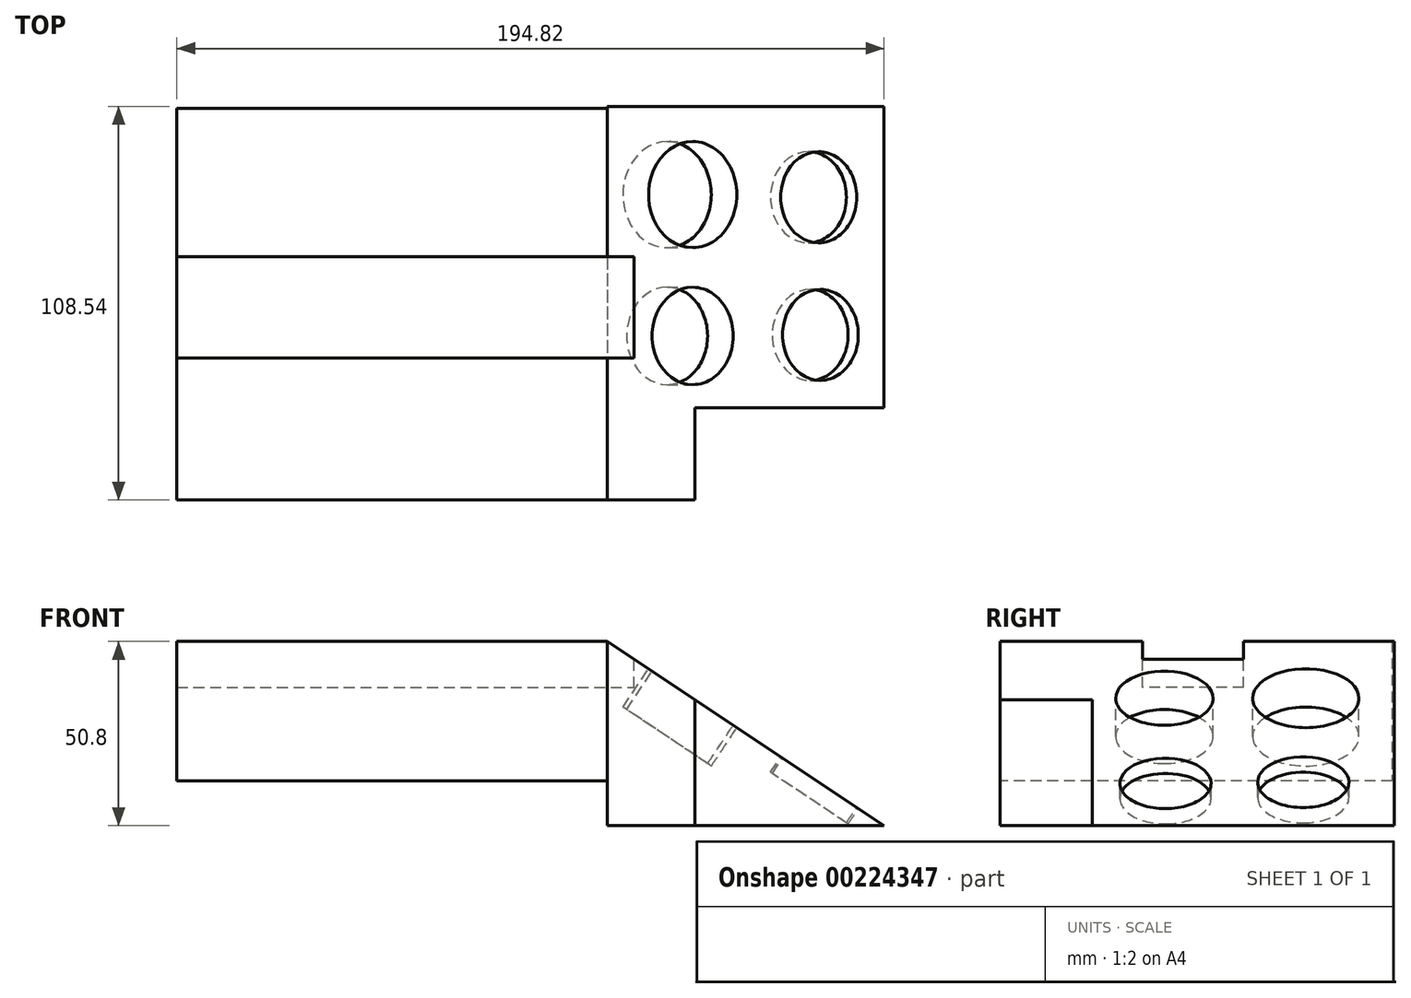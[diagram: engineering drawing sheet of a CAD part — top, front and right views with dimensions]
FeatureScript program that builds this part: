
annotation { "Feature Type Name" : "Feature", "Feature Type Description" : "" }
export const myFeature = defineFeature(function(context is Context, id is Id, definition is map)
    precondition{}
    {
        {
            var Q0;
            Q0=qCreatedBy(makeId("Top.planeOp"),FACE);
            var sketch = newSketch(context, id + "F0", { "sketchPlane" : qUnion([Q0])});
            skLineSegment(sketch, "E0.bottom", {"start": v(0, 41.45) * mm, "end": v(76.16, 41.45) * mm});
            skLineSegment(sketch, "E0.top", {"start": v(0, -67.09) * mm, "end": v(76.16, -67.09) * mm});
            skLineSegment(sketch, "E0.left", {"start": v(0, 41.45) * mm, "end": v(0, -67.09) * mm});
            skLineSegment(sketch, "E0.right", {"start": v(76.16, 41.45) * mm, "end": v(76.16, -67.09) * mm});
            skSolve(sketch);
        }
        {
            var Q0;
            Q0 = qSketchRegion(id + "F0", true);
            extrude(context, id + "F1", {"entities" : qUnion([Q0]), "depth" : 50.8 * mm});
        }
        {
            var Q0;
            Q0=makeQuery(id+"F1.opExtrude","SWEPT_FACE",FACE,{"disambiguationData":[OSD([sQuery(id+"F0.wireOp",EDGE,"E0.top")])]});
            var sketch = newSketch(context, id + "F2", { "sketchPlane" : qUnion([Q0])});
            skLineSegment(sketch, "E1", {"start": v(0, 50.8) * mm, "end": v(76.16, 0) * mm});
            skLineSegment(sketch, "E2", {"start": v(76.16, 0) * mm, "end": v(76.16, 50.8) * mm});
            skLineSegment(sketch, "E3", {"start": v(76.16, 50.8) * mm, "end": v(0, 50.8) * mm});
            skSolve(sketch);
        }
        {
            var Q0;
            Q0=makeQuery(id+"F2.imprint","IMPRINT",FACE,{"disambiguationData":[TD([[makeQuery(id+"F2.imprint","IMPRINT",EDGE,{"derivedFrom":sQuery(id+"F2.wireOp",EDGE,"E1")}),1.0]])]});
            extrude(context, id + "F3", {"entities" : qUnion([Q0]), "operationType" : NewBodyOperationType.REMOVE, "oppositeDirection" : true, "depth" : 118.87 * mm});
        }
        {
            var Q0;
            Q0=makeQuery(id+"F1.opExtrude","SWEPT_FACE",FACE,{"disambiguationData":[OSD([sQuery(id+"F0.wireOp",EDGE,"E0.top")])]});
            var sketch = newSketch(context, id + "F4", { "sketchPlane" : qUnion([Q0])});
            skLineSegment(sketch, "E4", {"start": v(24.07, 34.74) * mm, "end": v(24.07, 0) * mm});
            skLineSegment(sketch, "E5", {"start": v(76.16, 0) * mm, "end": v(24.07, 34.74) * mm});
            skSolve(sketch);
        }
        {
            var Q0;
            Q0 = qSketchRegion(id + "F4", true);
            var Q1;
            {var subQ0=sQuery(id+"F4.wireOp",EDGE,"E4");Q1=makeQuery(id+"F4.imprint","IMPRINT",FACE,{"disambiguationData":[TD([[makeQuery(id+"F4.imprint","IMPRINT",EDGE,{"derivedFrom":subQ0}),1.0]])]});}
            extrude(context, id + "F5", {"entities" : qUnion([Q0, Q1]), "operationType" : NewBodyOperationType.REMOVE, "oppositeDirection" : true, "depth" : 25.4 * mm});
        }
        {
            var Q0;
            Q0=makeQuery(id+"F3.boolean.opBoolean","COPY",FACE,{"derivedFrom":makeQuery(id+"F3.opExtrude","SWEPT_FACE",FACE,{"disambiguationData":[OSD([sQuery(id+"F2.wireOp",EDGE,"E1")])]})});
            var sketch = newSketch(context, id + "F6", { "sketchPlane" : qUnion([Q0])});
            skCircle(sketch, "E6", {"center": v(42.3, -21.54) * mm, "radius": 12.55 * mm});
            skSolve(sketch);
        }
        {
            var Q0;
            Q0 = qSketchRegion(id + "F6", true);
            extrude(context, id + "F7", {"entities" : qUnion([Q0]), "operationType" : NewBodyOperationType.REMOVE, "oppositeDirection" : true, "depth" : 5.08 * mm});
        }
        {
            var Q0;
            Q0=makeQuery(id+"F3.boolean.opBoolean","COPY",FACE,{"derivedFrom":makeQuery(id+"F3.opExtrude","SWEPT_FACE",FACE,{"disambiguationData":[OSD([sQuery(id+"F2.wireOp",EDGE,"E1")])]})});
            var sketch = newSketch(context, id + "F8", { "sketchPlane" : qUnion([Q0])});
            skCircle(sketch, "E7", {"center": v(41.72, 16.4) * mm, "radius": 12.57 * mm});
            skSolve(sketch);
        }
        {
            var Q0;
            Q0 = qSketchRegion(id + "F8", true);
            extrude(context, id + "F9", {"entities" : qUnion([Q0]), "operationType" : NewBodyOperationType.REMOVE, "oppositeDirection" : true, "depth" : 5.08 * mm});
        }
        {
            var Q0;
            Q0=makeQuery(id+"F3.boolean.opBoolean","COPY",FACE,{"derivedFrom":makeQuery(id+"F3.opExtrude","SWEPT_FACE",FACE,{"disambiguationData":[OSD([sQuery(id+"F2.wireOp",EDGE,"E1")])]})});
            var sketch = newSketch(context, id + "F10", { "sketchPlane" : qUnion([Q0])});
            skCircle(sketch, "E8", {"center": v(0, -21.84) * mm, "radius": 13.43 * mm});
            skSolve(sketch);
        }
        {
            var Q0;
            Q0 = qSketchRegion(id + "F10", true);
            extrude(context, id + "F11", {"entities" : qUnion([Q0]), "operationType" : NewBodyOperationType.REMOVE, "oppositeDirection" : true, "depth" : 12.7 * mm});
        }
        {
            var Q0;
            Q0=makeQuery(id+"F3.boolean.opBoolean","COPY",FACE,{"derivedFrom":makeQuery(id+"F3.opExtrude","SWEPT_FACE",FACE,{"disambiguationData":[OSD([sQuery(id+"F2.wireOp",EDGE,"E1")])]})});
            var sketch = newSketch(context, id + "F12", { "sketchPlane" : qUnion([Q0])});
            skCircle(sketch, "E9", {"center": v(0, 17.12) * mm, "radius": 14.63 * mm});
            skSolve(sketch);
        }
        {
            var Q0;
            Q0 = qSketchRegion(id + "F12", true);
            extrude(context, id + "F13", {"entities" : qUnion([Q0]), "operationType" : NewBodyOperationType.REMOVE, "oppositeDirection" : true, "depth" : 12.7 * mm});
        }
        {
            var Q0;
            Q0=qCreatedBy(makeId("Top.planeOp"),FACE);
            var sketch = newSketch(context, id + "F14", { "sketchPlane" : qUnion([Q0])});
            skLineSegment(sketch, "E10.bottom", {"start": v(0, 40.9) * mm, "end": v(-118.66, 40.9) * mm});
            skLineSegment(sketch, "E10.top", {"start": v(0, -67) * mm, "end": v(-118.66, -67) * mm});
            skLineSegment(sketch, "E10.left", {"start": v(0, 40.9) * mm, "end": v(0, -67) * mm});
            skLineSegment(sketch, "E10.right", {"start": v(-118.66, 40.9) * mm, "end": v(-118.66, -67) * mm});
            skSolve(sketch);
        }
        {
            var Q0;
            Q0 = qSketchRegion(id + "F14", true);
            extrude(context, id + "F15", {"entities" : qUnion([Q0]), "operationType" : NewBodyOperationType.ADD, "depth" : 50.8 * mm});
        }
        {
            var Q0;
            Q0=makeQuery(id+"F15.opExtrude","CAP_FACE",FACE,{"disambiguationData":[OSD([sQuery(id+"F14.wireOp",EDGE,"E10.bottom"),sQuery(id+"F14.wireOp",EDGE,"E10.top"),sQuery(id+"F14.wireOp",EDGE,"E10.left"),sQuery(id+"F14.wireOp",EDGE,"E10.right")])],"isStart":false});
            var sketch = newSketch(context, id + "F16", { "sketchPlane" : qUnion([Q0])});
            skLineSegment(sketch, "E11.bottom", {"start": v(-118.66, 0) * mm, "end": v(7.37, 0) * mm});
            skLineSegment(sketch, "E11.top", {"start": v(-118.66, -27.91) * mm, "end": v(7.37, -27.91) * mm});
            skLineSegment(sketch, "E11.left", {"start": v(-118.66, 0) * mm, "end": v(-118.66, -27.91) * mm});
            skLineSegment(sketch, "E11.right", {"start": v(7.37, 0) * mm, "end": v(7.37, -27.91) * mm});
            skSolve(sketch);
        }
        {
            var Q0;
            Q0 = qSketchRegion(id + "F16", true);
            extrude(context, id + "F17", {"entities" : qUnion([Q0]), "operationType" : NewBodyOperationType.REMOVE, "oppositeDirection" : true, "depth" : 12.7 * mm});
        }
        {
            var Q0;
            Q0=makeQuery(id+"F15.opExtrude","SWEPT_FACE",FACE,{"disambiguationData":[OSD([sQuery(id+"F14.wireOp",EDGE,"E10.top")])]});
            var sketch = newSketch(context, id + "F18", { "sketchPlane" : qUnion([Q0])});
            skLineSegment(sketch, "E12.bottom", {"start": v(-118.66, 0) * mm, "end": v(0, 0) * mm});
            skLineSegment(sketch, "E12.top", {"start": v(-118.66, 12.4) * mm, "end": v(0, 12.4) * mm});
            skLineSegment(sketch, "E12.left", {"start": v(-118.66, 0) * mm, "end": v(-118.66, 12.4) * mm});
            skLineSegment(sketch, "E12.right", {"start": v(0, 0) * mm, "end": v(0, 12.4) * mm});
            skSolve(sketch);
        }
        {
            var Q0;
            Q0 = qSketchRegion(id + "F18", true);
            extrude(context, id + "F19", {"entities" : qUnion([Q0]), "operationType" : NewBodyOperationType.REMOVE, "oppositeDirection" : true, "depth" : 143.76 * mm});
        }
    });
